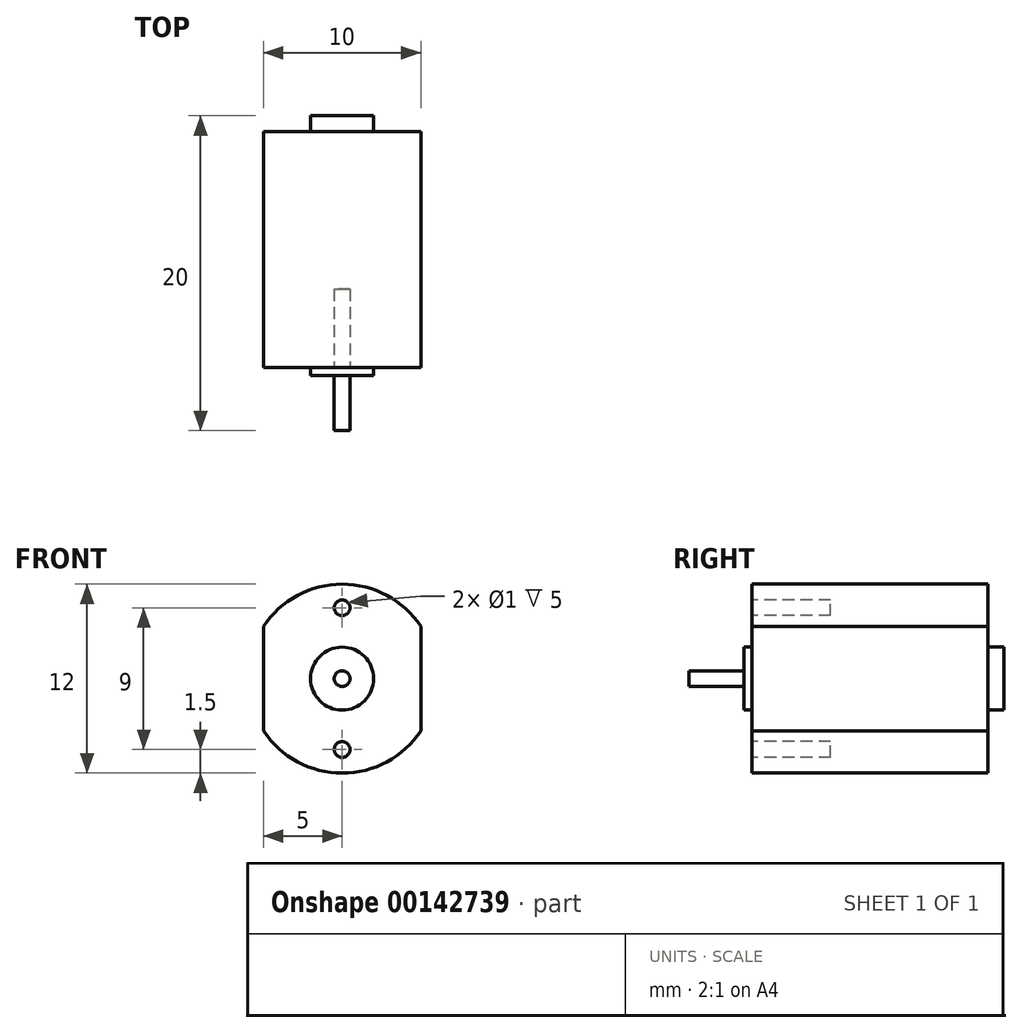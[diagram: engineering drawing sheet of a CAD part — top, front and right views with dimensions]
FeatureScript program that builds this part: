
annotation { "Feature Type Name" : "Feature", "Feature Type Description" : "" }
export const myFeature = defineFeature(function(context is Context, id is Id, definition is map)
    precondition{}
    {
        {
            var Q0;
            Q0=qCreatedBy(makeId("Front.planeOp"),FACE);
            var sketch = newSketch(context, id + "F0", { "sketchPlane" : qUnion([Q0])});
            skArc(sketch, "E0", {"start": v(-5, -3.32) * mm, "mid": v(0, -6) * mm, "end": v(5, -3.32) * mm});
            skLineSegment(sketch, "E1", {"start": v(0, 6) * mm, "end": v(0, -6) * mm, "construction": true});
            skLineSegment(sketch, "E2", {"start": v(-5, 3.32) * mm, "end": v(-5, -3.32) * mm});
            skLineSegment(sketch, "E3.MirrorCS", {"start": v(5, 3.32) * mm, "end": v(5, -3.32) * mm});
            skArc(sketch, "E4.trimOffspring", {"start": v(5, 3.32) * mm, "mid": v(0, 6) * mm, "end": v(-5, 3.32) * mm});
            skSolve(sketch);
        }
        {
            var Q0;
            Q0 = qSketchRegion(id + "F0", true);
            extrude(context, id + "F1", {"entities" : qUnion([Q0]), "endBound" : BoundingType.SYMMETRIC, "depth" : 15 * mm});
        }
        {
            var Q0;
            Q0=makeQuery(id+"F1.opExtrude","CAP_FACE",FACE,{"disambiguationData":[OSD([sQuery(id+"F0.wireOp",EDGE,"E0"),sQuery(id+"F0.wireOp",EDGE,"E2"),sQuery(id+"F0.wireOp",EDGE,"E3.MirrorCS"),sQuery(id+"F0.wireOp",EDGE,"E4.trimOffspring")])],"isStart":false});
            var sketch = newSketch(context, id + "F2", { "sketchPlane" : qUnion([Q0])});
            skCircle(sketch, "E5", {"center": v(0, 0) * mm, "radius": 0.5 * mm});
            skSolve(sketch);
        }
        {
            var Q0;
            Q0 = qSketchRegion(id + "F2", true);
            extrude(context, id + "F3", {"entities" : qUnion([Q0]), "operationType" : NewBodyOperationType.ADD, "depth" : 4 * mm});
        }
        {
            var Q0;
            Q0=makeQuery(id+"F1.opExtrude","CAP_FACE",FACE,{"disambiguationData":[OSD([sQuery(id+"F0.wireOp",EDGE,"E0"),sQuery(id+"F0.wireOp",EDGE,"E2"),sQuery(id+"F0.wireOp",EDGE,"E3.MirrorCS"),sQuery(id+"F0.wireOp",EDGE,"E4.trimOffspring")])],"isStart":false});
            var sketch = newSketch(context, id + "F4", { "sketchPlane" : qUnion([Q0])});
            skCircle(sketch, "E6", {"center": v(0, 0) * mm, "radius": 2 * mm});
            skSolve(sketch);
        }
        {
            var Q0;
            Q0 = qSketchRegion(id + "F4", true);
            extrude(context, id + "F5", {"entities" : qUnion([Q0]), "operationType" : NewBodyOperationType.ADD, "depth" : .5 * mm});
        }
        {
            var Q0;
            Q0=makeQuery(id+"F1.opExtrude","CAP_FACE",FACE,{"disambiguationData":[OSD([sQuery(id+"F0.wireOp",EDGE,"E0"),sQuery(id+"F0.wireOp",EDGE,"E2"),sQuery(id+"F0.wireOp",EDGE,"E3.MirrorCS"),sQuery(id+"F0.wireOp",EDGE,"E4.trimOffspring")])],"isStart":true});
            var sketch = newSketch(context, id + "F6", { "sketchPlane" : qUnion([Q0])});
            skCircle(sketch, "E7", {"center": v(0, 0) * mm, "radius": 2 * mm});
            skSolve(sketch);
        }
        {
            var Q0;
            Q0 = qSketchRegion(id + "F6", true);
            extrude(context, id + "F7", {"entities" : qUnion([Q0]), "operationType" : NewBodyOperationType.ADD, "depth" : 1 * mm});
        }
        {
            var Q0;
            Q0=makeQuery(id+"F1.opExtrude","CAP_FACE",FACE,{"disambiguationData":[OSD([sQuery(id+"F0.wireOp",EDGE,"E0"),sQuery(id+"F0.wireOp",EDGE,"E2"),sQuery(id+"F0.wireOp",EDGE,"E3.MirrorCS"),sQuery(id+"F0.wireOp",EDGE,"E4.trimOffspring")])],"isStart":false});
            var sketch = newSketch(context, id + "F8", { "sketchPlane" : qUnion([Q0])});
            skCircle(sketch, "E8", {"center": v(0, 4.5) * mm, "radius": 0.5 * mm});
            skLineSegment(sketch, "E9", {"start": v(-5, 0) * mm, "end": v(5, 0) * mm, "construction": true});
            skCircle(sketch, "E10.MirrorC", {"center": v(0, -4.5) * mm, "radius": 0.5 * mm});
            skSolve(sketch);
        }
        {
            var Q0;
            Q0 = qSketchRegion(id + "F8", true);
            extrude(context, id + "F9", {"entities" : qUnion([Q0]), "operationType" : NewBodyOperationType.REMOVE, "oppositeDirection" : true, "depth" : 5 * mm});
        }
    });
